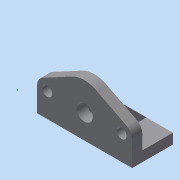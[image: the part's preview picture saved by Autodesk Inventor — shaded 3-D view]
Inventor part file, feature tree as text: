
AUTODESK INVENTOR PART (.ipt)
format: ipt  version: 2015 (Build 190159000, 159)  size: 359,424 bytes
history: native  units: in
note: dims shown in document units (in); Inventor stores cm internally (conversion verified against a paired STEP export)
features: sketch x17, extrude x13, hole x3, projected_geometry x2, mirror x1, fillet x1, chamfer x1, other x1
ambient origin geometry x8: Origin, YZ Plane, XZ Plane, XY Plane, X Axis, Y Axis, Z Axis, Center Point
bodies: Solid1 (feature_tree)
feature tree (39):
  extrude  "Extrusion1"  Depth=1.9685in
  sketch  "Sketch2"  dims[d2=0.7874in d3=0.0in d4=0.1969in]
  extrude  "Extrusion2"  Depth=0.1969in
  extrude  "Extrusion3"  Depth=0.1969in TaperAngle=0.0deg
  extrude  "Extrusion5"  Depth=0.1969in
  hole  "Hole1"  [1 undecoded]
  hole  "Hole2"  [1 undecoded]
  hole  "Hole3"  [1 undecoded]
  extrude  "Extrusion6"  Depth=0.5906in
  extrude  "Extrusion7"  Depth=0.5906in
  mirror  "Mirror1"
  sketch  "Sketch9"  dims[d30=0.5906in d31=0.4724in]
  fillet  "Fillet1"  Radius=0.3937in
  extrude  "Extrusion8"  Depth=0.3937in
  sketch  "Sketch11"  dims[d41=0.3937in d42=0.4724in]
  extrude  "Extrusion9"  Depth=0.1969in TaperAngle=0.0deg
  extrude  "Extrusion10"  TaperAngle=0.0deg  [1 undecoded]
  extrude  "Extrusion11"  Depth=0.344in
  chamfer  "Chamfer1"  Distance=0.333in
  extrude  "Extrusion12"  TaperAngle=0.0deg  [1 undecoded]
  extrude  "Extrusion13"  Depth=0.5906in TaperAngle=0.0deg
  extrude  "Extrusion14"  Depth=0.5906in TaperAngle=0.0deg
  sketch  "Sketch1"  dims[d0=1.9685in d1=1.9685in]
  sketch  "Sketch3"  dims[d5=0.1969in d6=0.2953in d7=0.0in]
  sketch  "Sketch4"  dims[d8=0.1969in d9=0.0in d12=0.5in]
  sketch  "Sketch5"  dims[d13=0.5in d14=0.0in d15=0.0in]
  sketch  "Sketch6"  dims[d17=0.2756in]
  sketch  "Sketch7"  dims[d20=0.315in d21=0.75in d22=0.375in d23=0.25in d24=0.5635in d25=1.0in d26=0.8108in d27=0.2756in]
  sketch  "Sketch8"  dims[d28=0.3937in d29=0.3937in]
  sketch  "Sketch10"  dims[d32=0.1969in d33=0.75in d34=0.375in d35=0.25in d36=0.5635in d37=1.0in d38=0.8108in d39=0.5906in d40=0.3937in]
  other  "Image1"
  sketch  "Sketch12"  dims[d43=0.1969in d44=0.75in d45=0.375in d46=0.25in d47=0.5635in d48=1.0in d49=0.8108in d50=1.0in d51=0.0in]
  sketch  "Sketch13"  dims[d52=0.0in d53=0.0in d54=0.0in]
  sketch  "Sketch14"  dims[d55=0.315in d56=0.344in]
  sketch  "Sketch15"  dims[d57=0.333in]
  projected_geometry  "Projected Loop1"
  sketch  "Sketch16"  dims[d58=0.5in]
  projected_geometry  "Projected Loop2"
  sketch  "Sketch17"  dims[d59=0.5in d60=0.333in d61=0.0in d62=1.0in d63=0.0in d79=1.0in d80=0.0in d81=1.0in d82=0.0in d83=0.3937in d84=0.1969in d85=0.3937in d86=0.1969in d87=0.5906in d88=0.0in d89=0.5906in d90=0.0787in d91=45.0deg d92=0.1181in d93=0.0in d94=0.1181in d95=0.0in d96=0.0in d97=0.0in]
note: 5 required parameter values undecoded (feature->parameter linkage not recoverable at this tier; creation-order binding heuristic only, values carry confidence <= 0.55)
